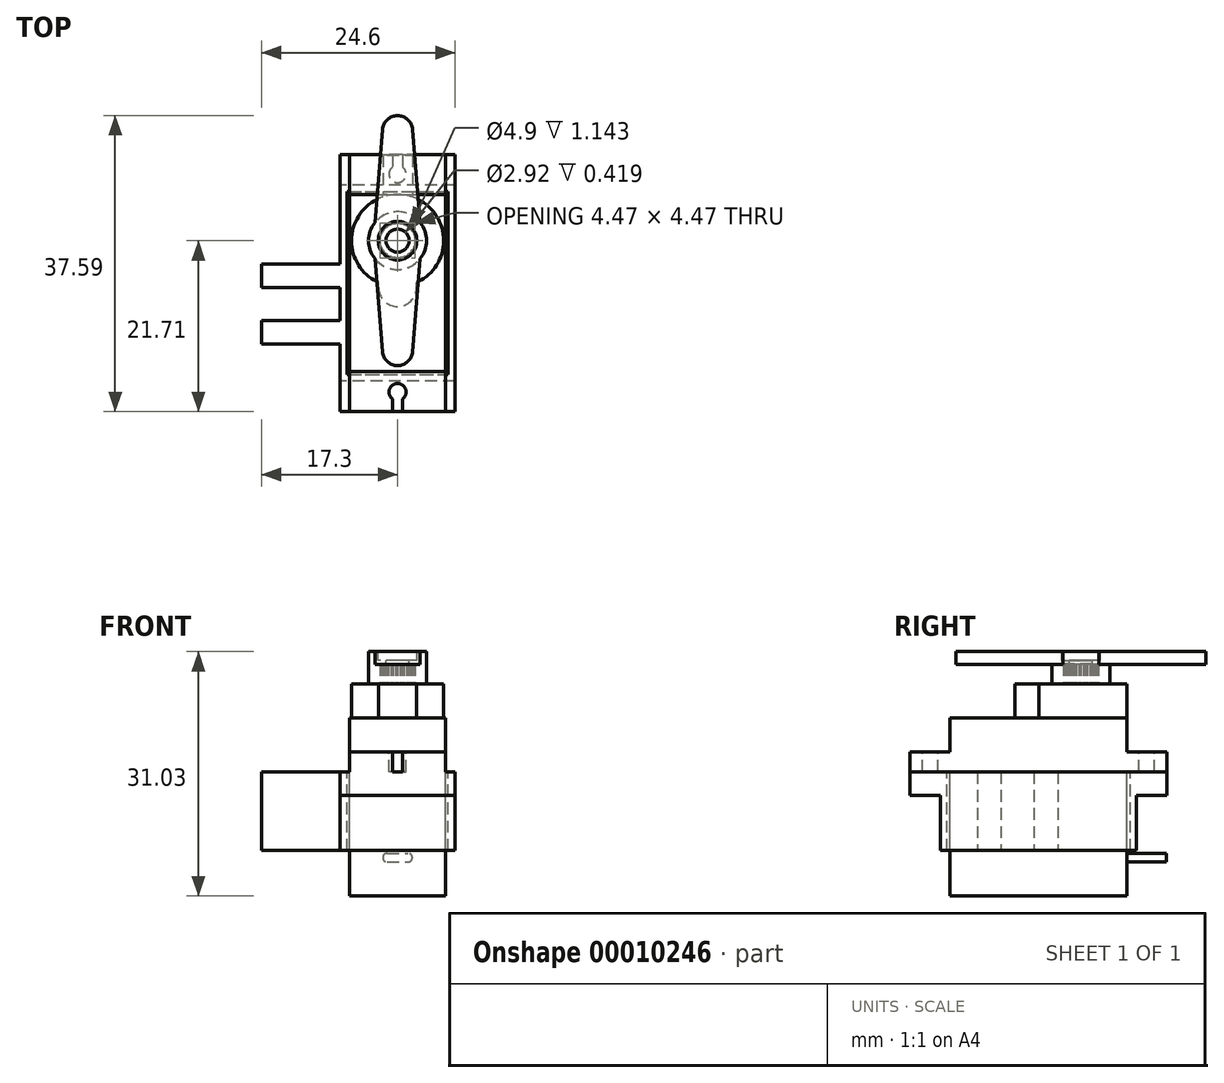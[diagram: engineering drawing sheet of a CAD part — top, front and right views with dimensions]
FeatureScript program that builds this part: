
annotation { "Feature Type Name" : "Feature", "Feature Type Description" : "" }
export const myFeature = defineFeature(function(context is Context, id is Id, definition is map)
    precondition{}
    {
        {
            var Q0;
            Q0=qCreatedBy(makeId("Top.planeOp"),FACE);
            var sketch = newSketch(context, id + "F0", { "sketchPlane" : qUnion([Q0])});
            skArc(sketch, "E0", {"start": v(2.41, -5.33) * mm, "mid": v(0, 5.85) * mm, "end": v(-2.41, -5.33) * mm});
            skArc(sketch, "E1", {"start": v(-2.41, -5.96) * mm, "mid": v(0, -8.37) * mm, "end": v(2.41, -5.96) * mm});
            skLineSegment(sketch, "E2", {"start": v(-2.41, -5.96) * mm, "end": v(-2.41, -5.33) * mm});
            skLineSegment(sketch, "E3", {"start": v(2.41, -5.96) * mm, "end": v(2.41, -5.33) * mm});
            skPoint(sketch, "E4", {"position": v(0, 5.85) * mm});
            skPoint(sketch, "E5", {"position": v(0, -8.37) * mm});
            skSolve(sketch);
        }
        {
            var Q0;
            Q0=qSketchRegion(id+"F0",true);
            extrude(context, id + "F1", {"entities" : qUnion([Q0]), "depth" : 4.32 * mm});
        }
        {
            var Q0;
            Q0=makeQuery(id+"F1.opExtrude","CAP_FACE",FACE,{"disambiguationData":[OSD([sQuery(id+"F0.wireOp",EDGE,"E0"),sQuery(id+"F0.wireOp",EDGE,"E1"),sQuery(id+"F0.wireOp",EDGE,"E2"),sQuery(id+"F0.wireOp",EDGE,"E3")])],"isStart":false});
            var sketch = newSketch(context, id + "F2", { "sketchPlane" : qUnion([Q0])});
            skCircle(sketch, "E6.cCircle", {"center": v(0, 0) * mm, "radius": 2.16 * mm, "construction": true});
            skLineSegment(sketch, "E6.0", {"start": v(2.16, 0.58) * mm, "end": v(2.16, 0.28) * mm});
            skLineSegment(sketch, "E6.1", {"start": v(2.16, -0.58) * mm, "end": v(2.01, -0.83) * mm});
            skLineSegment(sketch, "E6.2", {"start": v(1.58, -1.58) * mm, "end": v(1.33, -1.73) * mm});
            skLineSegment(sketch, "E6.3", {"start": v(0.58, -2.16) * mm, "end": v(0.28, -2.16) * mm});
            skLineSegment(sketch, "E6.4", {"start": v(-0.58, -2.16) * mm, "end": v(-0.83, -2.01) * mm});
            skLineSegment(sketch, "E6.5", {"start": v(-1.58, -1.58) * mm, "end": v(-1.73, -1.33) * mm});
            skLineSegment(sketch, "E6.6", {"start": v(-2.16, -0.58) * mm, "end": v(-2.16, -0.28) * mm});
            skLineSegment(sketch, "E6.7", {"start": v(-2.16, 0.58) * mm, "end": v(-2.01, 0.83) * mm});
            skLineSegment(sketch, "E6.8", {"start": v(-1.58, 1.58) * mm, "end": v(-1.33, 1.73) * mm});
            skLineSegment(sketch, "E6.9", {"start": v(-0.58, 2.16) * mm, "end": v(-0.28, 2.16) * mm});
            skLineSegment(sketch, "E6.10", {"start": v(0.58, 2.16) * mm, "end": v(0.83, 2.01) * mm});
            skLineSegment(sketch, "E6.11", {"start": v(1.58, 1.58) * mm, "end": v(1.73, 1.33) * mm});
            skPoint(sketch, "E6.0.midPoint", {"position": v(2.16, 0) * mm});
            skLineSegment(sketch, "E7.0", {"start": v(1.94, 1.12) * mm, "end": v(2.01, 0.83) * mm});
            skLineSegment(sketch, "E7.1", {"start": v(2.24, 0) * mm, "end": v(2.16, -0.28) * mm});
            skLineSegment(sketch, "E7.2", {"start": v(1.94, -1.12) * mm, "end": v(1.73, -1.33) * mm});
            skLineSegment(sketch, "E7.3", {"start": v(1.12, -1.94) * mm, "end": v(0.83, -2.01) * mm});
            skLineSegment(sketch, "E7.4", {"start": v(0, -2.24) * mm, "end": v(-0.28, -2.16) * mm});
            skLineSegment(sketch, "E7.5", {"start": v(-1.12, -1.94) * mm, "end": v(-1.33, -1.73) * mm});
            skLineSegment(sketch, "E7.6", {"start": v(-1.94, -1.12) * mm, "end": v(-2.01, -0.83) * mm});
            skLineSegment(sketch, "E7.7", {"start": v(-2.24, 0) * mm, "end": v(-2.16, 0.28) * mm});
            skLineSegment(sketch, "E7.8", {"start": v(-1.94, 1.12) * mm, "end": v(-1.73, 1.33) * mm});
            skLineSegment(sketch, "E7.9", {"start": v(-1.12, 1.94) * mm, "end": v(-0.83, 2.01) * mm});
            skLineSegment(sketch, "E7.10", {"start": v(0, 2.24) * mm, "end": v(0.28, 2.16) * mm});
            skLineSegment(sketch, "E7.11", {"start": v(1.12, 1.94) * mm, "end": v(1.33, 1.73) * mm});
            skPoint(sketch, "E7.0.midPoint", {"position": v(2.09, 0.56) * mm});
            skLineSegment(sketch, "E8", {"start": v(0, 0) * mm, "end": v(2.09, 0.56) * mm});
            skLineSegment(sketch, "E9.trimOffspring", {"start": v(2.01, 0.83) * mm, "end": v(2.16, 0.58) * mm});
            skLineSegment(sketch, "E10.trimOffspring", {"start": v(2.16, 0.28) * mm, "end": v(2.24, 0) * mm});
            skLineSegment(sketch, "E11.trimOffspring", {"start": v(2.16, -0.28) * mm, "end": v(2.16, -0.58) * mm});
            skLineSegment(sketch, "E12.trimOffspring", {"start": v(1.73, 1.33) * mm, "end": v(1.94, 1.12) * mm});
            skLineSegment(sketch, "E13.trimOffspring", {"start": v(1.33, 1.73) * mm, "end": v(1.58, 1.58) * mm});
            skLineSegment(sketch, "E14.trimOffspring", {"start": v(2.01, -0.83) * mm, "end": v(1.94, -1.12) * mm});
            skLineSegment(sketch, "E15.trimOffspring", {"start": v(1.73, -1.33) * mm, "end": v(1.58, -1.58) * mm});
            skLineSegment(sketch, "E16.trimOffspring", {"start": v(1.33, -1.73) * mm, "end": v(1.12, -1.94) * mm});
            skLineSegment(sketch, "E17.trimOffspring", {"start": v(0.83, -2.01) * mm, "end": v(0.58, -2.16) * mm});
            skLineSegment(sketch, "E18.trimOffspring", {"start": v(0.28, -2.16) * mm, "end": v(0, -2.24) * mm});
            skLineSegment(sketch, "E19.trimOffspring", {"start": v(-0.28, -2.16) * mm, "end": v(-0.58, -2.16) * mm});
            skLineSegment(sketch, "E20.trimOffspring", {"start": v(-0.83, -2.01) * mm, "end": v(-1.12, -1.94) * mm});
            skLineSegment(sketch, "E21.trimOffspring", {"start": v(-1.33, -1.73) * mm, "end": v(-1.58, -1.58) * mm});
            skLineSegment(sketch, "E22.trimOffspring", {"start": v(-1.73, -1.33) * mm, "end": v(-1.94, -1.12) * mm});
            skLineSegment(sketch, "E23.trimOffspring", {"start": v(-2.01, -0.83) * mm, "end": v(-2.16, -0.58) * mm});
            skLineSegment(sketch, "E24.trimOffspring", {"start": v(-2.16, -0.28) * mm, "end": v(-2.24, 0) * mm});
            skLineSegment(sketch, "E25.trimOffspring", {"start": v(-2.16, 0.28) * mm, "end": v(-2.16, 0.58) * mm});
            skLineSegment(sketch, "E26.trimOffspring", {"start": v(0.83, 2.01) * mm, "end": v(1.12, 1.94) * mm});
            skLineSegment(sketch, "E27.trimOffspring", {"start": v(0.28, 2.16) * mm, "end": v(0.58, 2.16) * mm});
            skLineSegment(sketch, "E28.trimOffspring", {"start": v(-0.28, 2.16) * mm, "end": v(0, 2.24) * mm});
            skLineSegment(sketch, "E29.trimOffspring", {"start": v(-0.83, 2.01) * mm, "end": v(-0.58, 2.16) * mm});
            skLineSegment(sketch, "E30.trimOffspring", {"start": v(-1.33, 1.73) * mm, "end": v(-1.12, 1.94) * mm});
            skLineSegment(sketch, "E31.trimOffspring", {"start": v(-1.73, 1.33) * mm, "end": v(-1.58, 1.58) * mm});
            skLineSegment(sketch, "E32.trimOffspring", {"start": v(-2.01, 0.83) * mm, "end": v(-1.94, 1.12) * mm});
            skSolve(sketch);
        }
        {
            var Q0;
            Q0=qSketchRegion(id+"F2",true);
            extrude(context, id + "F3", {"entities" : qUnion([Q0]), "operationType" : NewBodyOperationType.ADD, "depth" : 2.54 * mm});
        }
        {
            var Q0;
            Q0=makeQuery(id+"F1.opExtrude","CAP_FACE",FACE,{"disambiguationData":[OSD([sQuery(id+"F0.wireOp",EDGE,"E0"),sQuery(id+"F0.wireOp",EDGE,"E1"),sQuery(id+"F0.wireOp",EDGE,"E2"),sQuery(id+"F0.wireOp",EDGE,"E3")])],"isStart":true});
            var sketch = newSketch(context, id + "F4", { "sketchPlane" : qUnion([Q0])});
            skLineSegment(sketch, "E33.bottom", {"start": v(-6.1, -5.85) * mm, "end": v(6.1, -5.85) * mm});
            skLineSegment(sketch, "E33.top", {"start": v(-6.1, 16.63) * mm, "end": v(6.1, 16.63) * mm});
            skLineSegment(sketch, "E33.left", {"start": v(-6.1, -5.85) * mm, "end": v(-6.1, 16.63) * mm});
            skLineSegment(sketch, "E33.right", {"start": v(6.1, -5.85) * mm, "end": v(6.1, 16.63) * mm});
            skPoint(sketch, "E34", {"position": v(0, -5.85) * mm});
            skSolve(sketch);
        }
        {
            var Q0;
            Q0=qSketchRegion(id+"F4",true);
            extrude(context, id + "F5", {"entities" : qUnion([Q0]), "operationType" : NewBodyOperationType.ADD, "depth" : 22.6 * mm});
        }
        {
            var Q0;
            Q0=makeQuery(id+"F5.opExtrude","CAP_FACE",FACE,{"disambiguationData":[OSD([sQuery(id+"F4.wireOp",EDGE,"E33.bottom"),sQuery(id+"F4.wireOp",EDGE,"E33.top"),sQuery(id+"F4.wireOp",EDGE,"E33.left"),sQuery(id+"F4.wireOp",EDGE,"E33.right")])],"isStart":false});
            cPlane(context, id + "F6", {"entities" : qUnion([Q0]), "cplaneType" : CPlaneType.OFFSET, "offset" : 18.29 * mm, "oppositeDirection" : true, "width" : 152.4 * mm, "height" : 152.4 * mm});
        }
        {
            var Q0;
            Q0=qCreatedBy(id+"F6.planeOp",FACE);
            var sketch = newSketch(context, id + "F7", { "sketchPlane" : qUnion([Q0])});
            skLineSegment(sketch, "E35.bottom", {"start": v(-6.1, -5.85) * mm, "end": v(6.1, -5.85) * mm});
            skLineSegment(sketch, "E35.top", {"start": v(-6.1, -10.93) * mm, "end": v(6.1, -10.93) * mm});
            skLineSegment(sketch, "E35.left", {"start": v(-6.1, -5.85) * mm, "end": v(-6.1, -10.93) * mm});
            skLineSegment(sketch, "E35.right", {"start": v(6.1, -5.85) * mm, "end": v(6.1, -10.93) * mm});
            skLineSegment(sketch, "E36.bottom", {"start": v(6.1, 16.63) * mm, "end": v(-6.1, 16.63) * mm});
            skLineSegment(sketch, "E36.top", {"start": v(6.1, 21.7) * mm, "end": v(-6.1, 21.7) * mm});
            skLineSegment(sketch, "E36.left", {"start": v(6.1, 16.63) * mm, "end": v(6.1, 21.7) * mm});
            skLineSegment(sketch, "E36.right", {"start": v(-6.1, 16.63) * mm, "end": v(-6.1, 21.7) * mm});
            skSolve(sketch);
        }
        {
            var Q0;
            Q0=qSketchRegion(id+"F7",true);
            extrude(context, id + "F8", {"entities" : qUnion([Q0]), "operationType" : NewBodyOperationType.ADD, "depth" : 2.54 * mm});
        }
        {
            var Q0;
            Q0=makeQuery(id+"F8.opExtrude","CAP_FACE",FACE,{"disambiguationData":[OSD([sQuery(id+"F7.wireOp",EDGE,"E35.bottom"),sQuery(id+"F7.wireOp",EDGE,"E35.top"),sQuery(id+"F7.wireOp",EDGE,"E35.left"),sQuery(id+"F7.wireOp",EDGE,"E35.right")])],"isStart":true});
            var sketch = newSketch(context, id + "F9", { "sketchPlane" : qUnion([Q0])});
            skArc(sketch, "E37", {"start": v(-0.64, 9.33) * mm, "mid": v(0, 7.37) * mm, "end": v(0.64, 9.33) * mm});
            skArc(sketch, "E38", {"start": v(0.64, -20.1) * mm, "mid": v(0, -18.15) * mm, "end": v(-0.64, -20.1) * mm});
            skLineSegment(sketch, "E39", {"start": v(0.64, 10.93) * mm, "end": v(0.64, 9.33) * mm});
            skLineSegment(sketch, "E40", {"start": v(-0.64, 10.93) * mm, "end": v(-0.64, 9.33) * mm});
            skLineSegment(sketch, "E41", {"start": v(0.64, -20.1) * mm, "end": v(0.64, -21.7) * mm});
            skLineSegment(sketch, "E42", {"start": v(-0.64, -21.7) * mm, "end": v(-0.64, -20.1) * mm});
            skLineSegment(sketch, "E43", {"start": v(-0.64, -21.7) * mm, "end": v(0.64, -21.7) * mm});
            skLineSegment(sketch, "E44", {"start": v(-0.64, 10.93) * mm, "end": v(0.64, 10.93) * mm});
            skSolve(sketch);
        }
        {
            var Q0;
            Q0=qSketchRegion(id+"F9",true);
            extrude(context, id + "F10", {"entities" : qUnion([Q0]), "operationType" : NewBodyOperationType.REMOVE, "endBound" : BoundingType.UP_TO_NEXT, "oppositeDirection" : true, "depth" : 25.4 * mm});
        }
        {
            var Q0;
            Q0=makeQuery(id+"F1.opExtrude","CAP_FACE",FACE,{"disambiguationData":[OSD([sQuery(id+"F0.wireOp",EDGE,"E0"),sQuery(id+"F0.wireOp",EDGE,"E1"),sQuery(id+"F0.wireOp",EDGE,"E2"),sQuery(id+"F0.wireOp",EDGE,"E3")])],"isStart":false});
            var sketch = newSketch(context, id + "F11", { "sketchPlane" : qUnion([Q0])});
            skCircle(sketch, "E45", {"center": v(0, 0) * mm, "radius": 3.67 * mm});
            skSolve(sketch);
        }
        {
            var Q0;
            Q0=qSketchRegion(id+"F11",true);
            extrude(context, id + "F12", {"entities" : qUnion([Q0]), "depth" : 4.1 * mm});
        }
        {
            var Q0;
            Q0=makeQuery(id+"F12.opExtrude","CAP_FACE",FACE,{"disambiguationData":[OSD([sQuery(id+"F11.wireOp",EDGE,"E45")])],"isStart":false});
            var sketch = newSketch(context, id + "F13", { "sketchPlane" : qUnion([Q0])});
            skCircle(sketch, "E46", {"center": v(0, 0) * mm, "radius": 1.46 * mm});
            skSolve(sketch);
        }
        {
            var Q0;
            Q0=qSketchRegion(id+"F13",true);
            extrude(context, id + "F14", {"entities" : qUnion([Q0]), "operationType" : NewBodyOperationType.REMOVE, "endBound" : BoundingType.UP_TO_NEXT, "oppositeDirection" : true, "depth" : 25.4 * mm});
        }
        {
            var Q0;
            Q0=makeQuery(id+"F12.opExtrude","CAP_FACE",FACE,{"disambiguationData":[OSD([sQuery(id+"F11.wireOp",EDGE,"E45")])],"isStart":false});
            var sketch = newSketch(context, id + "F15", { "sketchPlane" : qUnion([Q0])});
            skCircle(sketch, "E47", {"center": v(0, 0) * mm, "radius": 2.45 * mm});
            skSolve(sketch);
        }
        {
            var Q0;
            Q0=qSketchRegion(id+"F15",true);
            extrude(context, id + "F16", {"entities" : qUnion([Q0]), "operationType" : NewBodyOperationType.REMOVE, "oppositeDirection" : true, "depth" : 1.14 * mm});
        }
        {
            var Q0;
            Q0=makeQuery(id+"F12.opExtrude","CAP_FACE",FACE,{"disambiguationData":[OSD([sQuery(id+"F11.wireOp",EDGE,"E45")])],"isStart":false});
            var sketch = newSketch(context, id + "F17", { "sketchPlane" : qUnion([Q0])});
            skArc(sketch, "E48", {"start": v(1.9, 14.12) * mm, "mid": v(0, 15.88) * mm, "end": v(-1.9, 14.12) * mm});
            skLineSegment(sketch, "E49", {"start": v(-1.9, 14.12) * mm, "end": v(-2.86, 2.3) * mm});
            skLineSegment(sketch, "E50", {"start": v(2.86, 2.3) * mm, "end": v(1.9, 14.12) * mm});
            skArc(sketch, "E51", {"start": v(2.86, 2.3) * mm, "mid": v(0, 3.67) * mm, "end": v(-2.86, 2.3) * mm});
            skLineSegment(sketch, "E52.MirrorCS", {"start": v(-1.9, -14.12) * mm, "end": v(-2.86, -2.3) * mm});
            skArc(sketch, "E53.MirrorC", {"start": v(1.9, -14.12) * mm, "mid": v(0, -15.88) * mm, "end": v(-1.9, -14.12) * mm});
            skLineSegment(sketch, "E54.MirrorCS", {"start": v(2.86, -2.3) * mm, "end": v(1.9, -14.12) * mm});
            skArc(sketch, "E55.MirrorCS", {"start": v(2.86, -2.3) * mm, "mid": v(0, -3.67) * mm, "end": v(-2.86, -2.3) * mm});
            skSolve(sketch);
        }
        {
            var Q0;
            Q0=qSketchRegion(id+"F17",true);
            extrude(context, id + "F18", {"entities" : qUnion([Q0]), "operationType" : NewBodyOperationType.ADD, "oppositeDirection" : true, "depth" : 1.6 * mm});
        }
        {
            var Q0;
            Q0=makeQuery(id+"F8.opExtrude","CAP_FACE",FACE,{"disambiguationData":[OSD([sQuery(id+"F7.wireOp",EDGE,"E35.bottom"),sQuery(id+"F7.wireOp",EDGE,"E35.top"),sQuery(id+"F7.wireOp",EDGE,"E35.left"),sQuery(id+"F7.wireOp",EDGE,"E35.right")])],"isStart":false});
            var sketch = newSketch(context, id + "F19", { "sketchPlane" : qUnion([Q0])});
            skLineSegment(sketch, "E56.0", {"start": v(7.3, -7.05) * mm, "end": v(7.3, 17.83) * mm});
            skLineSegment(sketch, "E56.1", {"start": v(-7.3, -7.05) * mm, "end": v(7.3, -7.05) * mm});
            skLineSegment(sketch, "E56.2", {"start": v(-7.3, -7.05) * mm, "end": v(-7.3, 17.83) * mm});
            skLineSegment(sketch, "E56.3", {"start": v(-7.3, 17.83) * mm, "end": v(7.3, 17.83) * mm});
            skLineSegment(sketch, "E57.0", {"start": v(6.4, -6.25) * mm, "end": v(6.4, 17.03) * mm});
            skLineSegment(sketch, "E57.1", {"start": v(-6.4, -6.25) * mm, "end": v(6.4, -6.25) * mm});
            skLineSegment(sketch, "E57.2", {"start": v(-6.4, -6.25) * mm, "end": v(-6.4, 17.03) * mm});
            skLineSegment(sketch, "E57.3", {"start": v(-6.4, 17.03) * mm, "end": v(6.4, 17.03) * mm});
            skSolve(sketch);
        }
        {
            var Q0;
            Q0 = qSketchRegion(id + "F19", true);
            extrude(context, id + "F20", {"entities" : qUnion([Q0]), "depth" : 10 * mm});
        }
        {
            var Q0;
            Q0=makeQuery(id+"F8.opExtrude","CAP_FACE",FACE,{"disambiguationData":[OSD([sQuery(id+"F7.wireOp",EDGE,"E36.bottom"),sQuery(id+"F7.wireOp",EDGE,"E36.top"),sQuery(id+"F7.wireOp",EDGE,"E36.left"),sQuery(id+"F7.wireOp",EDGE,"E36.right")])],"isStart":false});
            var sketch = newSketch(context, id + "F21", { "sketchPlane" : qUnion([Q0])});
            skLineSegment(sketch, "E58.bottom", {"start": v(7.3, 17.83) * mm, "end": v(-7.3, 17.83) * mm});
            skLineSegment(sketch, "E58.top", {"start": v(7.3, 21.7) * mm, "end": v(-7.3, 21.7) * mm});
            skLineSegment(sketch, "E58.left", {"start": v(7.3, 17.83) * mm, "end": v(7.3, 21.7) * mm});
            skLineSegment(sketch, "E58.right", {"start": v(-7.3, 17.83) * mm, "end": v(-7.3, 21.7) * mm});
            skLineSegment(sketch, "E59.bottom", {"start": v(7.3, -7.05) * mm, "end": v(-7.3, -7.05) * mm});
            skLineSegment(sketch, "E59.top", {"start": v(7.3, -10.93) * mm, "end": v(-7.3, -10.93) * mm});
            skLineSegment(sketch, "E59.left", {"start": v(7.3, -7.05) * mm, "end": v(7.3, -10.93) * mm});
            skLineSegment(sketch, "E59.right", {"start": v(-7.3, -7.05) * mm, "end": v(-7.3, -10.93) * mm});
            skSolve(sketch);
        }
        {
            var Q0;
            Q0 = qSketchRegion(id + "F21", true);
            extrude(context, id + "F22", {"entities" : qUnion([Q0]), "operationType" : NewBodyOperationType.ADD, "depth" : 3 * mm});
        }
        {
            var Q0;
            Q0=makeQuery(id+"F22.boolean.opBoolean","MERGE",FACE,{"derivedFrom":[makeQuery(id+"F20.opExtrude","SWEPT_FACE",FACE,{"disambiguationData":[OSD([sQuery(id+"F19.wireOp",EDGE,"E56.2")])]}),makeQuery(id+"F22.opExtrude","SWEPT_FACE",FACE,{"disambiguationData":[OSD([sQuery(id+"F21.wireOp",EDGE,"E58.right")])]}),makeQuery(id+"F22.opExtrude","SWEPT_FACE",FACE,{"disambiguationData":[OSD([sQuery(id+"F21.wireOp",EDGE,"E59.right")])]})]});
            var sketch = newSketch(context, id + "F23", { "sketchPlane" : qUnion([Q0])});
            skLineSegment(sketch, "E60.bottom", {"start": v(2.95, -6.86) * mm, "end": v(5.95, -6.86) * mm});
            skLineSegment(sketch, "E60.top", {"start": v(2.95, -16.86) * mm, "end": v(5.95, -16.86) * mm});
            skLineSegment(sketch, "E60.left", {"start": v(2.95, -6.86) * mm, "end": v(2.95, -16.86) * mm});
            skLineSegment(sketch, "E60.right", {"start": v(5.95, -6.86) * mm, "end": v(5.95, -16.86) * mm});
            skLineSegment(sketch, "E61.bottom", {"start": v(13.15, -6.86) * mm, "end": v(10.15, -6.86) * mm});
            skLineSegment(sketch, "E61.top", {"start": v(13.15, -16.86) * mm, "end": v(10.15, -16.86) * mm});
            skLineSegment(sketch, "E61.left", {"start": v(13.15, -6.86) * mm, "end": v(13.15, -16.86) * mm});
            skLineSegment(sketch, "E61.right", {"start": v(10.15, -6.86) * mm, "end": v(10.15, -16.86) * mm});
            skSolve(sketch);
        }
        {
            var Q0;
            Q0 = qSketchRegion(id + "F23", true);
            extrude(context, id + "F24", {"entities" : qUnion([Q0]), "operationType" : NewBodyOperationType.ADD, "depth" : 10 * mm});
        }
        {
            var Q0;
            Q0=makeQuery(id+"F1.opExtrude","SWEPT_BODY",BODY,{"disambiguationData":[OSD([sQuery(id+"F0.wireOp",EDGE,"E0"),sQuery(id+"F0.wireOp",EDGE,"E1"),sQuery(id+"F0.wireOp",EDGE,"E2"),sQuery(id+"F0.wireOp",EDGE,"E3")])]});
            var Q1;
            Q1=makeQuery(id+"F12.opExtrude","SWEPT_BODY",BODY,{"disambiguationData":[OSD([sQuery(id+"F11.wireOp",EDGE,"E45")])]});
            booleanBodies(context, id + "F25", {"operationType" : BooleanOperationType.SUBTRACTION, "tools" : qUnion([Q0]), "targets" : qUnion([Q1]), "keepTools" : true});
        }
        {
            var Q0;
            {var subQ0=sQuery(id+"F4.wireOp",EDGE,"E33.bottom");var subQ3=sQuery(id+"F4.wireOp",EDGE,"E33.right");var subQ4=sQuery(id+"F4.wireOp",EDGE,"E33.left");Q0=makeQuery(id+"F8.boolean.opBoolean","SPLIT",FACE,{"disambiguationData":[TD([makeQuery(id+"F5.opExtrude","CAP_FACE",FACE,{"disambiguationData":[OSD([subQ0,sQuery(id+"F4.wireOp",EDGE,"E33.top"),subQ4,subQ3])],"isStart":false})])],"derivedFrom":makeQuery(id+"F5.opExtrude","SWEPT_FACE",FACE,{"disambiguationData":[OSD([subQ0])]})});}
            var sketch = newSketch(context, id + "F26", { "sketchPlane" : qUnion([Q0])});
            skLineSegment(sketch, "E62.bottom", {"start": v(1.32, -18.3) * mm, "end": v(-1.33, -18.3) * mm});
            skLineSegment(sketch, "E62.top", {"start": v(1.32, -17.2) * mm, "end": v(-1.33, -17.2) * mm});
            skArc(sketch, "E63", {"start": v(-1.33, -17.2) * mm, "mid": v(-1.88, -17.76) * mm, "end": v(-1.33, -18.3) * mm});
            skArc(sketch, "E64", {"start": v(1.32, -18.3) * mm, "mid": v(1.87, -17.76) * mm, "end": v(1.32, -17.2) * mm});
            skPoint(sketch, "E65", {"position": v(0, -18.3) * mm});
            skSolve(sketch);
        }
        {
            var Q0;
            Q0 = qSketchRegion(id + "F26", true);
            extrude(context, id + "F27", {"entities" : qUnion([Q0]), "depth" : 5 * mm});
        }
    });
